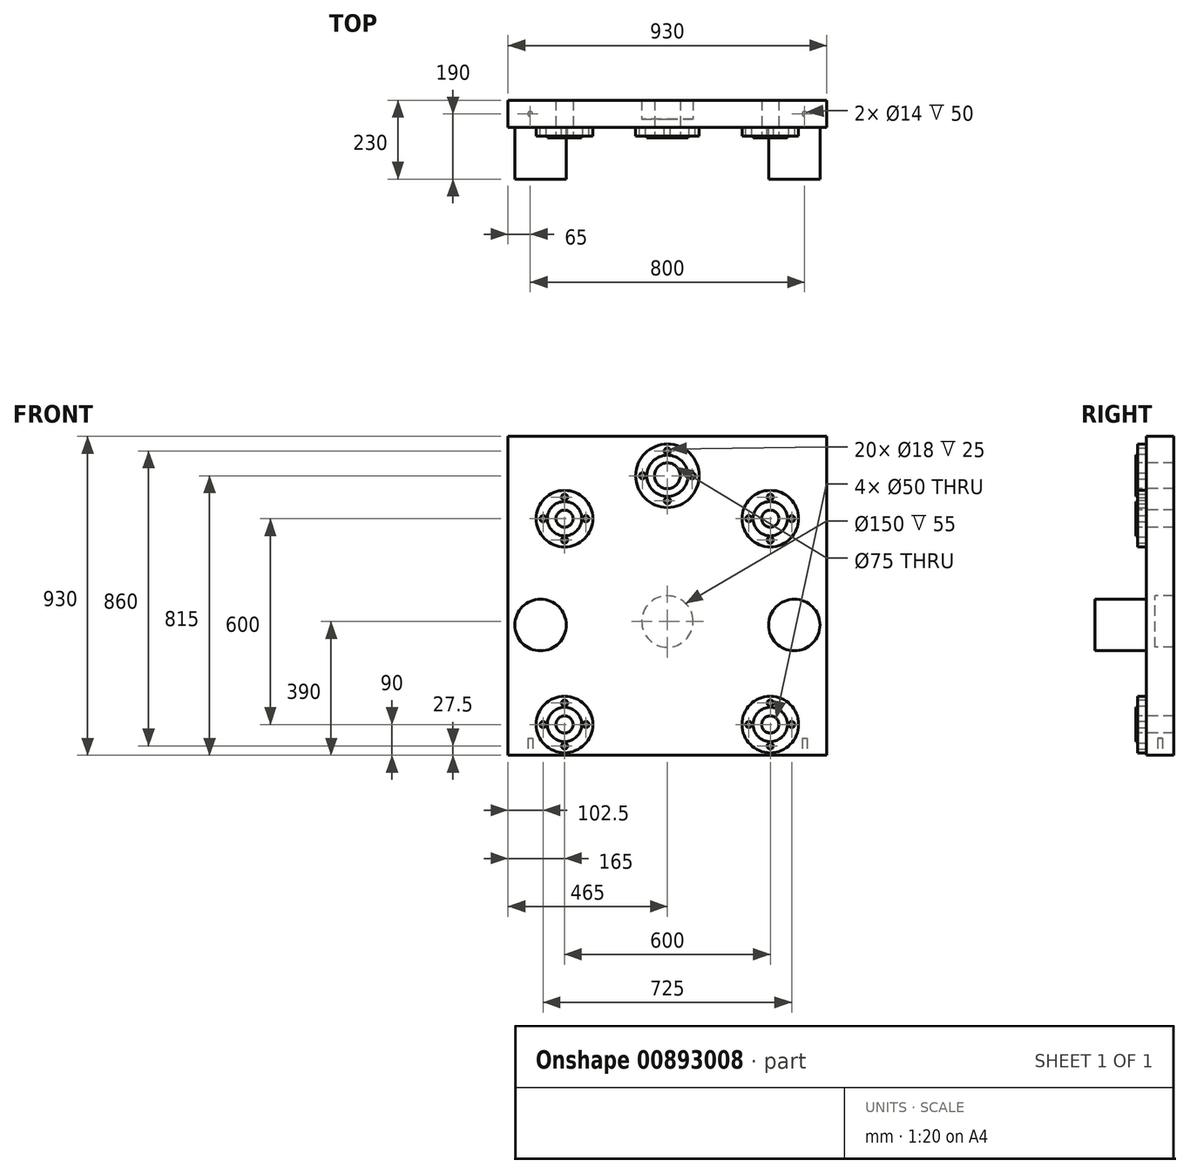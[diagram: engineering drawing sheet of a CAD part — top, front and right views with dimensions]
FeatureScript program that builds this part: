
annotation { "Feature Type Name" : "Feature", "Feature Type Description" : "" }
export const myFeature = defineFeature(function(context is Context, id is Id, definition is map)
    precondition{}
    {
        {
            var Q0;
            Q0=qCreatedBy(makeId("Front.planeOp"),FACE);
            var sketch = newSketch(context, id + "F0", { "sketchPlane" : qUnion([Q0])});
            skLineSegment(sketch, "E0.bottom", {"start": v(465, -965) * mm, "end": v(345, -965) * mm});
            skLineSegment(sketch, "E0.top", {"start": v(465, 965) * mm, "end": v(-465, 965) * mm});
            skLineSegment(sketch, "E0.left", {"start": v(465, -965) * mm, "end": v(465, 965) * mm});
            skLineSegment(sketch, "E0.right", {"start": v(-465, -965) * mm, "end": v(-465, 965) * mm});
            skPoint(sketch, "E0.middle", {"position": v(0, 0) * mm});
            skLineSegment(sketch, "E1.top", {"start": v(-345, -765) * mm, "end": v(345, -765) * mm});
            skLineSegment(sketch, "E1.left", {"start": v(-345, -965) * mm, "end": v(-345, -765) * mm});
            skLineSegment(sketch, "E1.right", {"start": v(345, -965) * mm, "end": v(345, -765) * mm});
            skLineSegment(sketch, "E2.bottom", {"start": v(-345, -645) * mm, "end": v(345, -645) * mm});
            skLineSegment(sketch, "E2.top", {"start": v(-345, -295) * mm, "end": v(345, -295) * mm});
            skLineSegment(sketch, "E2.left", {"start": v(-345, -645) * mm, "end": v(-345, -295) * mm});
            skLineSegment(sketch, "E2.right", {"start": v(345, -645) * mm, "end": v(345, -295) * mm});
            skLineSegment(sketch, "E3.trimOffspring", {"start": v(-345, -965) * mm, "end": v(-465, -965) * mm});
            skLineSegment(sketch, "E4.bottom", {"start": v(-345, -175) * mm, "end": v(345, -175) * mm});
            skLineSegment(sketch, "E4.top", {"start": v(-345, 25) * mm, "end": v(345, 25) * mm});
            skLineSegment(sketch, "E4.left", {"start": v(-345, -175) * mm, "end": v(-345, 25) * mm});
            skLineSegment(sketch, "E4.right", {"start": v(345, -175) * mm, "end": v(345, 25) * mm});
            skPoint(sketch, "E5.middle", {"position": v(0, 425) * mm});
            skSolve(sketch);
        }
        {
            var Q0;
            Q0=makeQuery(id+"F0.imprint","IMPRINT",FACE,{"disambiguationData":[TD([[makeQuery(id+"F0.imprint","IMPRINT",EDGE,{"derivedFrom":sQuery(id+"F0.wireOp",EDGE,"E0.bottom")}),-1.0]])]});
            extrude(context, id + "F1", {"entities" : qUnion([Q0]), "depth" : 80 * mm, "offsetDistance" : 25 * mm});
        }
        {
            var Q0;
            Q0=makeQuery(id+"F1.opExtrude","CAP_FACE",FACE,{"disambiguationData":[OSD([sQuery(id+"F0.wireOp",EDGE,"E0.bottom"),sQuery(id+"F0.wireOp",EDGE,"E0.top"),sQuery(id+"F0.wireOp",EDGE,"E0.left"),sQuery(id+"F0.wireOp",EDGE,"E0.right"),sQuery(id+"F0.wireOp",EDGE,"E1.top"),sQuery(id+"F0.wireOp",EDGE,"E1.left"),sQuery(id+"F0.wireOp",EDGE,"E1.right"),sQuery(id+"F0.wireOp",EDGE,"E2.bottom"),sQuery(id+"F0.wireOp",EDGE,"E2.top"),sQuery(id+"F0.wireOp",EDGE,"E2.left"),sQuery(id+"F0.wireOp",EDGE,"E2.right"),sQuery(id+"F0.wireOp",EDGE,"E3.trimOffspring"),sQuery(id+"F0.wireOp",EDGE,"nSGubIzk-R7de-6MO4-penA-cvBglKJnvsGC"),sQuery(id+"F0.wireOp",EDGE,"E4.bottom"),sQuery(id+"F0.wireOp",EDGE,"E4.top"),sQuery(id+"F0.wireOp",EDGE,"E4.left"),sQuery(id+"F0.wireOp",EDGE,"E4.right")])],"isStart":false});
            var sketch = newSketch(context, id + "F2", { "sketchPlane" : qUnion([Q0])});
            skCircle(sketch, "E6", {"center": v(-300, 125) * mm, "radius": 25 * mm});
            skCircle(sketch, "E7.0", {"center": v(0, 425) * mm, "radius": 75 * mm});
            skCircle(sketch, "E8.0.1.0", {"center": v(-300, 725) * mm, "radius": 25 * mm});
            skCircle(sketch, "E8.1.0.0", {"center": v(300, 125) * mm, "radius": 25 * mm});
            skCircle(sketch, "E8.1.1.0", {"center": v(300, 725) * mm, "radius": 25 * mm});
            skLineSegment(sketch, "E8.direction1", {"start": v(-300, 125) * mm, "end": v(300, 125) * mm, "construction": true});
            skLineSegment(sketch, "E8.direction2", {"start": v(-300, 125) * mm, "end": v(-300, 725) * mm, "construction": true});
            skSolve(sketch);
        }
        {
            var Q0;
            Q0=qSketchRegion(id+"F2",true);
            extrude(context, id + "F3", {"entities" : qUnion([Q0]), "operationType" : NewBodyOperationType.REMOVE, "oppositeDirection" : true, "depth" : 100 * mm, "offsetDistance" : 25 * mm});
        }
        {
            var Q0;
            Q0=makeQuery(id+"F1.opExtrude","CAP_FACE",FACE,{"disambiguationData":[OSD([sQuery(id+"F0.wireOp",EDGE,"E0.bottom"),sQuery(id+"F0.wireOp",EDGE,"E0.top"),sQuery(id+"F0.wireOp",EDGE,"E0.left"),sQuery(id+"F0.wireOp",EDGE,"E0.right"),sQuery(id+"F0.wireOp",EDGE,"E1.top"),sQuery(id+"F0.wireOp",EDGE,"E1.left"),sQuery(id+"F0.wireOp",EDGE,"E1.right"),sQuery(id+"F0.wireOp",EDGE,"E2.bottom"),sQuery(id+"F0.wireOp",EDGE,"E2.top"),sQuery(id+"F0.wireOp",EDGE,"E2.left"),sQuery(id+"F0.wireOp",EDGE,"E2.right"),sQuery(id+"F0.wireOp",EDGE,"E3.trimOffspring"),sQuery(id+"F0.wireOp",EDGE,"nSGubIzk-R7de-6MO4-penA-cvBglKJnvsGC"),sQuery(id+"F0.wireOp",EDGE,"E4.bottom"),sQuery(id+"F0.wireOp",EDGE,"E4.top"),sQuery(id+"F0.wireOp",EDGE,"E4.left"),sQuery(id+"F0.wireOp",EDGE,"E4.right")])],"isStart":false});
            var sketch = newSketch(context, id + "F4", { "sketchPlane" : qUnion([Q0])});
            skCircle(sketch, "E9", {"center": v(-370, 415) * mm, "radius": 75 * mm});
            skCircle(sketch, "E10.MirrorC", {"center": v(370, 415) * mm, "radius": 75 * mm});
            skSolve(sketch);
        }
        {
            var Q0;
            Q0=qSketchRegion(id+"F4",true);
            extrude(context, id + "F5", {"entities" : qUnion([Q0]), "operationType" : NewBodyOperationType.ADD, "depth" : 150 * mm, "offsetDistance" : 25 * mm});
        }
        {
            var Q0;
            Q0=makeQuery(id+"F1.opExtrude","CAP_FACE",FACE,{"disambiguationData":[OSD([sQuery(id+"F0.wireOp",EDGE,"E0.bottom"),sQuery(id+"F0.wireOp",EDGE,"E0.top"),sQuery(id+"F0.wireOp",EDGE,"E0.left"),sQuery(id+"F0.wireOp",EDGE,"E0.right"),sQuery(id+"F0.wireOp",EDGE,"E1.top"),sQuery(id+"F0.wireOp",EDGE,"E1.left"),sQuery(id+"F0.wireOp",EDGE,"E1.right"),sQuery(id+"F0.wireOp",EDGE,"E2.bottom"),sQuery(id+"F0.wireOp",EDGE,"E2.top"),sQuery(id+"F0.wireOp",EDGE,"E2.left"),sQuery(id+"F0.wireOp",EDGE,"E2.right"),sQuery(id+"F0.wireOp",EDGE,"E3.trimOffspring"),sQuery(id+"F0.wireOp",EDGE,"nSGubIzk-R7de-6MO4-penA-cvBglKJnvsGC"),sQuery(id+"F0.wireOp",EDGE,"E4.bottom"),sQuery(id+"F0.wireOp",EDGE,"E4.top"),sQuery(id+"F0.wireOp",EDGE,"E4.left"),sQuery(id+"F0.wireOp",EDGE,"E4.right")])],"isStart":false});
            var sketch = newSketch(context, id + "F6", { "sketchPlane" : qUnion([Q0])});
            skCircle(sketch, "E11", {"center": v(-300, 725) * mm, "radius": 82.5 * mm});
            skCircle(sketch, "E12", {"center": v(-300, 787.5) * mm, "radius": 9 * mm});
            skCircle(sketch, "E13.0", {"center": v(-300, 725) * mm, "radius": 25 * mm});
            skCircle(sketch, "E14.1.0", {"center": v(-362.5, 725) * mm, "radius": 9 * mm});
            skCircle(sketch, "E14.2.0", {"center": v(-300, 662.5) * mm, "radius": 9 * mm});
            skCircle(sketch, "E14.3.0", {"center": v(-237.5, 725) * mm, "radius": 9 * mm});
            skPoint(sketch, "E15.0.1.0", {"position": v(-300, 125) * mm});
            skCircle(sketch, "E15.0.1.1", {"center": v(-300, 125) * mm, "radius": 82.5 * mm});
            skCircle(sketch, "E15.0.1.2", {"center": v(-300, 125) * mm, "radius": 25 * mm});
            skCircle(sketch, "E15.0.1.3", {"center": v(-237.5, 125) * mm, "radius": 9 * mm});
            skCircle(sketch, "E15.0.1.4", {"center": v(-362.5, 125) * mm, "radius": 9 * mm});
            skCircle(sketch, "E15.0.1.5", {"center": v(-300, 187.5) * mm, "radius": 9 * mm});
            skCircle(sketch, "E15.0.1.6", {"center": v(-300, 62.5) * mm, "radius": 9 * mm});
            skPoint(sketch, "E15.1.0.0", {"position": v(300, 725) * mm});
            skCircle(sketch, "E15.1.0.1", {"center": v(300, 725) * mm, "radius": 82.5 * mm});
            skCircle(sketch, "E15.1.0.2", {"center": v(300, 725) * mm, "radius": 25 * mm});
            skCircle(sketch, "E15.1.0.3", {"center": v(362.5, 725) * mm, "radius": 9 * mm});
            skCircle(sketch, "E15.1.0.4", {"center": v(237.5, 725) * mm, "radius": 9 * mm});
            skCircle(sketch, "E15.1.0.5", {"center": v(300, 787.5) * mm, "radius": 9 * mm});
            skCircle(sketch, "E15.1.0.6", {"center": v(300, 662.5) * mm, "radius": 9 * mm});
            skPoint(sketch, "E15.1.1.0", {"position": v(300, 125) * mm});
            skCircle(sketch, "E15.1.1.1", {"center": v(300, 125) * mm, "radius": 82.5 * mm});
            skCircle(sketch, "E15.1.1.2", {"center": v(300, 125) * mm, "radius": 25 * mm});
            skCircle(sketch, "E15.1.1.3", {"center": v(362.5, 125) * mm, "radius": 9 * mm});
            skCircle(sketch, "E15.1.1.4", {"center": v(237.5, 125) * mm, "radius": 9 * mm});
            skCircle(sketch, "E15.1.1.5", {"center": v(300, 187.5) * mm, "radius": 9 * mm});
            skCircle(sketch, "E15.1.1.6", {"center": v(300, 62.5) * mm, "radius": 9 * mm});
            skLineSegment(sketch, "E15.direction1", {"start": v(-300, 662.5) * mm, "end": v(300, 662.5) * mm, "construction": true});
            skLineSegment(sketch, "E15.direction2", {"start": v(-300, 662.5) * mm, "end": v(-300, 62.5) * mm, "construction": true});
            skSolve(sketch);
        }
        {
            var Q0;
            Q0=qSketchRegion(id+"F6",true);
            extrude(context, id + "F7", {"entities" : qUnion([Q0]), "operationType" : NewBodyOperationType.ADD, "depth" : 25 * mm, "offsetDistance" : 25 * mm});
        }
        {
            var Q0;
            Q0=makeQuery(id+"F7.opExtrude","CAP_FACE",FACE,{"disambiguationData":[OSD([sQuery(id+"F6.wireOp",EDGE,"E11"),sQuery(id+"F6.wireOp",EDGE,"E12"),sQuery(id+"F6.wireOp",EDGE,"E13.0"),sQuery(id+"F6.wireOp",EDGE,"E14.1.0"),sQuery(id+"F6.wireOp",EDGE,"E14.2.0"),sQuery(id+"F6.wireOp",EDGE,"E14.3.0")])],"isStart":false});
            var sketch = newSketch(context, id + "F8", { "sketchPlane" : qUnion([Q0])});
            skCircle(sketch, "E16", {"center": v(-300, 725) * mm, "radius": 50 * mm});
            skCircle(sketch, "E17.0.1.0", {"center": v(-300, 125) * mm, "radius": 50 * mm});
            skCircle(sketch, "E17.1.0.0", {"center": v(300, 725) * mm, "radius": 50 * mm});
            skCircle(sketch, "E17.1.1.0", {"center": v(300, 125) * mm, "radius": 50 * mm});
            skLineSegment(sketch, "E17.direction1", {"start": v(-300, 725) * mm, "end": v(300, 725) * mm, "construction": true});
            skLineSegment(sketch, "E17.direction2", {"start": v(-300, 725) * mm, "end": v(-300, 125) * mm, "construction": true});
            skCircle(sketch, "E18", {"center": v(300, 725) * mm, "radius": 25 * mm});
            skCircle(sketch, "E19", {"center": v(300, 125) * mm, "radius": 25 * mm});
            skCircle(sketch, "E20", {"center": v(-300, 125) * mm, "radius": 25 * mm});
            skCircle(sketch, "E21", {"center": v(-300, 725) * mm, "radius": 25 * mm});
            skSolve(sketch);
        }
        {
            var Q0;
            Q0=qSketchRegion(id+"F8",true);
            extrude(context, id + "F9", {"entities" : qUnion([Q0]), "operationType" : NewBodyOperationType.ADD, "depth" : 5 * mm, "offsetDistance" : 25 * mm});
        }
        {
            var Q0;
            {var subQ0=sQuery(id+"F0.wireOp",EDGE,"E4.right");var subQ1=sQuery(id+"F0.wireOp",EDGE,"E4.left");var subQ2=sQuery(id+"F0.wireOp",EDGE,"E4.top");var subQ3=sQuery(id+"F0.wireOp",EDGE,"E1.left");var subQ4=sQuery(id+"F0.wireOp",EDGE,"E4.bottom");var subQ5=sQuery(id+"F0.wireOp",EDGE,"E3.trimOffspring");var subQ6=sQuery(id+"F0.wireOp",EDGE,"E2.right");var subQ7=sQuery(id+"F0.wireOp",EDGE,"E0.left");var subQ8=sQuery(id+"F0.wireOp",EDGE,"E0.top");var subQ9=sQuery(id+"F0.wireOp",EDGE,"E0.right");var subQ10=sQuery(id+"F0.wireOp",EDGE,"E2.bottom");var subQ11=sQuery(id+"F0.wireOp",EDGE,"E0.bottom");var subQ12=sQuery(id+"F0.wireOp",EDGE,"E2.left");var subQ13=sQuery(id+"F0.wireOp",EDGE,"E1.top");var subQ14=sQuery(id+"F0.wireOp",EDGE,"E1.right");var subQ15=sQuery(id+"F0.wireOp",EDGE,"E2.top");Q0=makeQuery(id+"F7.boolean.opBoolean","SPLIT",FACE,{"disambiguationData":[TD([makeQuery(id+"F1.opExtrude","SWEPT_FACE",FACE,{"disambiguationData":[OSD([subQ11])]})])],"derivedFrom":makeQuery(id+"F1.opExtrude","CAP_FACE",FACE,{"disambiguationData":[OSD([subQ11,subQ8,subQ7,subQ9,subQ13,subQ3,subQ14,subQ10,subQ15,subQ12,subQ6,subQ5,subQ4,subQ2,subQ1,subQ0])],"isStart":false})});}
            var sketch = newSketch(context, id + "F10", { "sketchPlane" : qUnion([Q0])});
            skCircle(sketch, "E22.0", {"center": v(0, 425) * mm, "radius": 75 * mm});
            skSolve(sketch);
        }
        {
            var Q0;
            Q0=qSketchRegion(id+"F10",true);
            extrude(context, id + "F11", {"entities" : qUnion([Q0]), "operationType" : NewBodyOperationType.ADD, "oppositeDirection" : true, "depth" : 25 * mm, "offsetDistance" : 25 * mm});
        }
        {
            var Q0;
            {var subQ0=sQuery(id+"F0.wireOp",EDGE,"E4.right");var subQ1=sQuery(id+"F0.wireOp",EDGE,"E4.left");var subQ2=sQuery(id+"F0.wireOp",EDGE,"E4.top");var subQ3=sQuery(id+"F0.wireOp",EDGE,"E1.left");var subQ4=sQuery(id+"F0.wireOp",EDGE,"E4.bottom");var subQ5=sQuery(id+"F0.wireOp",EDGE,"E3.trimOffspring");var subQ6=sQuery(id+"F0.wireOp",EDGE,"E2.right");var subQ7=sQuery(id+"F0.wireOp",EDGE,"E0.left");var subQ8=sQuery(id+"F0.wireOp",EDGE,"E0.top");var subQ9=sQuery(id+"F0.wireOp",EDGE,"E0.right");var subQ10=sQuery(id+"F0.wireOp",EDGE,"E2.bottom");var subQ11=sQuery(id+"F0.wireOp",EDGE,"E0.bottom");var subQ12=sQuery(id+"F0.wireOp",EDGE,"E2.left");var subQ13=sQuery(id+"F0.wireOp",EDGE,"E1.top");var subQ14=sQuery(id+"F0.wireOp",EDGE,"E1.right");var subQ15=sQuery(id+"F0.wireOp",EDGE,"E2.top");Q0=makeQuery(id+"F11.boolean.opBoolean","MERGE",FACE,{"derivedFrom":[makeQuery(id+"F7.boolean.opBoolean","SPLIT",FACE,{"disambiguationData":[TD([makeQuery(id+"F1.opExtrude","SWEPT_FACE",FACE,{"disambiguationData":[OSD([subQ11])]})])],"derivedFrom":makeQuery(id+"F1.opExtrude","CAP_FACE",FACE,{"disambiguationData":[OSD([subQ11,subQ8,subQ7,subQ9,subQ13,subQ3,subQ14,subQ10,subQ15,subQ12,subQ6,subQ5,subQ4,subQ2,subQ1,subQ0])],"isStart":false})}),makeQuery(id+"F11.opExtrude","CAP_FACE",FACE,{"disambiguationData":[OSD([sQuery(id+"F10.wireOp",EDGE,"E22.0")])],"isStart":true})]});}
            var sketch = newSketch(context, id + "F12", { "sketchPlane" : qUnion([Q0])});
            skCircle(sketch, "E23", {"center": v(0, 850) * mm, "radius": 37.5 * mm});
            skPoint(sketch, "E23.centerSnap0", {"position": v(0, 965) * mm});
            skCircle(sketch, "E24.0", {"center": v(300, 725) * mm, "radius": 25 * mm});
            skSolve(sketch);
        }
        {
            var Q0;
            Q0=makeQuery(id+"F12.imprint","IMPRINT",FACE,{"disambiguationData":[TD([[makeQuery(id+"F12.imprint","IMPRINT",EDGE,{"derivedFrom":sQuery(id+"F12.wireOp",EDGE,"E23")}),1.0]])]});
            extrude(context, id + "F13", {"entities" : qUnion([Q0]), "operationType" : NewBodyOperationType.REMOVE, "oppositeDirection" : true, "depth" : 100 * mm, "offsetDistance" : 25 * mm});
        }
        {
            var Q0;
            {var subQ0=sQuery(id+"F0.wireOp",EDGE,"E4.right");var subQ1=sQuery(id+"F0.wireOp",EDGE,"E4.left");var subQ2=sQuery(id+"F0.wireOp",EDGE,"E4.top");var subQ3=sQuery(id+"F0.wireOp",EDGE,"E1.left");var subQ4=sQuery(id+"F0.wireOp",EDGE,"E4.bottom");var subQ5=sQuery(id+"F0.wireOp",EDGE,"E3.trimOffspring");var subQ6=sQuery(id+"F0.wireOp",EDGE,"E2.right");var subQ7=sQuery(id+"F0.wireOp",EDGE,"E0.left");var subQ8=sQuery(id+"F0.wireOp",EDGE,"E0.top");var subQ9=sQuery(id+"F0.wireOp",EDGE,"E0.right");var subQ10=sQuery(id+"F0.wireOp",EDGE,"E2.bottom");var subQ11=sQuery(id+"F0.wireOp",EDGE,"E0.bottom");var subQ12=sQuery(id+"F0.wireOp",EDGE,"E2.left");var subQ13=sQuery(id+"F0.wireOp",EDGE,"E1.top");var subQ14=sQuery(id+"F0.wireOp",EDGE,"E1.right");var subQ15=sQuery(id+"F0.wireOp",EDGE,"E2.top");Q0=makeQuery(id+"F11.boolean.opBoolean","MERGE",FACE,{"derivedFrom":[makeQuery(id+"F7.boolean.opBoolean","SPLIT",FACE,{"disambiguationData":[TD([makeQuery(id+"F1.opExtrude","SWEPT_FACE",FACE,{"disambiguationData":[OSD([subQ11])]})])],"derivedFrom":makeQuery(id+"F1.opExtrude","CAP_FACE",FACE,{"disambiguationData":[OSD([subQ11,subQ8,subQ7,subQ9,subQ13,subQ3,subQ14,subQ10,subQ15,subQ12,subQ6,subQ5,subQ4,subQ2,subQ1,subQ0])],"isStart":false})}),makeQuery(id+"F11.opExtrude","CAP_FACE",FACE,{"disambiguationData":[OSD([sQuery(id+"F10.wireOp",EDGE,"E22.0")])],"isStart":true})]});}
            var sketch = newSketch(context, id + "F14", { "sketchPlane" : qUnion([Q0])});
            skCircle(sketch, "E25", {"center": v(0, 850) * mm, "radius": 92.5 * mm});
            skCircle(sketch, "E26", {"center": v(0, 922.5) * mm, "radius": 9 * mm});
            skCircle(sketch, "E27.1.0", {"center": v(-72.5, 850) * mm, "radius": 9 * mm});
            skCircle(sketch, "E27.2.0", {"center": v(0, 777.5) * mm, "radius": 9 * mm});
            skCircle(sketch, "E27.3.0", {"center": v(72.5, 850) * mm, "radius": 9 * mm});
            skSolve(sketch);
        }
        {
            var Q0;
            Q0=makeQuery(id+"F14.imprint","IMPRINT",FACE,{"disambiguationData":[TD([[makeQuery(id+"F14.imprint","IMPRINT",EDGE,{"derivedFrom":sQuery(id+"F14.wireOp",EDGE,"E25")}),1.0]])]});
            extrude(context, id + "F15", {"entities" : qUnion([Q0]), "operationType" : NewBodyOperationType.ADD, "depth" : 25 * mm, "offsetDistance" : 25 * mm});
        }
        {
            var Q0;
            Q0=makeQuery(id+"F15.opExtrude","CAP_FACE",FACE,{"disambiguationData":[OSD([sQuery(id+"F12.wireOp",EDGE,"E23"),sQuery(id+"F14.wireOp",EDGE,"E25"),sQuery(id+"F14.wireOp",EDGE,"E26"),sQuery(id+"F14.wireOp",EDGE,"E27.1.0"),sQuery(id+"F14.wireOp",EDGE,"E27.2.0"),sQuery(id+"F14.wireOp",EDGE,"E27.3.0")])],"isStart":false});
            var sketch = newSketch(context, id + "F16", { "sketchPlane" : qUnion([Q0])});
            skCircle(sketch, "E28", {"center": v(0, 850) * mm, "radius": 60 * mm});
            skSolve(sketch);
        }
        {
            var Q0;
            Q0=makeQuery(id+"F16.imprint","IMPRINT",FACE,{"disambiguationData":[TD([[makeQuery(id+"F16.imprint","IMPRINT",EDGE,{"derivedFrom":sQuery(id+"F16.wireOp",EDGE,"E28")}),1.0]])]});
            extrude(context, id + "F17", {"entities" : qUnion([Q0]), "operationType" : NewBodyOperationType.ADD, "depth" : 5 * mm, "offsetDistance" : 25 * mm});
        }
        {
            var Q0;
            {var subQ2=sQuery(id+"F0.wireOp",EDGE,"E4.right");var subQ5=sQuery(id+"F0.wireOp",EDGE,"E4.left");var subQ8=sQuery(id+"F0.wireOp",EDGE,"E4.top");var subQ10=sQuery(id+"F0.wireOp",EDGE,"E4.bottom");var subQ12=sQuery(id+"F0.wireOp",EDGE,"E3.trimOffspring");var subQ14=sQuery(id+"F0.wireOp",EDGE,"E2.right");var subQ16=sQuery(id+"F0.wireOp",EDGE,"E0.left");var subQ18=sQuery(id+"F0.wireOp",EDGE,"E0.top");var subQ20=sQuery(id+"F0.wireOp",EDGE,"E0.right");var subQ23=sQuery(id+"F0.wireOp",EDGE,"E2.bottom");var subQ25=sQuery(id+"F0.wireOp",EDGE,"E0.bottom");var subQ26=makeQuery(id+"F1.opExtrude","SWEPT_FACE",FACE,{"disambiguationData":[OSD([subQ25])]});var subQ27=sQuery(id+"F0.wireOp",EDGE,"E2.left");var subQ29=sQuery(id+"F0.wireOp",EDGE,"E1.top");var subQ32=sQuery(id+"F0.wireOp",EDGE,"E1.left");var subQ34=sQuery(id+"F0.wireOp",EDGE,"E1.right");var subQ36=sQuery(id+"F0.wireOp",EDGE,"E2.top");Q0=makeQuery(id+"F15.boolean.opBoolean","SPLIT",FACE,{"disambiguationData":[TD([subQ26])],"derivedFrom":makeQuery(id+"F11.boolean.opBoolean","MERGE",FACE,{"derivedFrom":[makeQuery(id+"F7.boolean.opBoolean","SPLIT",FACE,{"disambiguationData":[TD([subQ26])],"derivedFrom":makeQuery(id+"F1.opExtrude","CAP_FACE",FACE,{"disambiguationData":[OSD([subQ25,subQ18,subQ16,subQ20,subQ29,subQ32,subQ34,subQ23,subQ36,subQ27,subQ14,subQ12,subQ10,subQ8,subQ5,subQ2])],"isStart":false})}),makeQuery(id+"F11.opExtrude","CAP_FACE",FACE,{"disambiguationData":[OSD([sQuery(id+"F10.wireOp",EDGE,"E22.0")])],"isStart":true})]})});}
            var sketch = newSketch(context, id + "F18", { "sketchPlane" : qUnion([Q0])});
            skLineSegment(sketch, "E29.bottom", {"start": v(-465, -965) * mm, "end": v(465, -965) * mm});
            skLineSegment(sketch, "E29.top", {"start": v(-465, 35) * mm, "end": v(465, 35) * mm});
            skLineSegment(sketch, "E29.left", {"start": v(-465, -965) * mm, "end": v(-465, 35) * mm});
            skLineSegment(sketch, "E29.right", {"start": v(465, -965) * mm, "end": v(465, 35) * mm});
            skSolve(sketch);
        }
        {
            var Q0;
            Q0=qSketchRegion(id+"F18",true);
            extrude(context, id + "F19", {"entities" : qUnion([Q0]), "operationType" : NewBodyOperationType.REMOVE, "oppositeDirection" : true, "depth" : 100 * mm, "offsetDistance" : 25 * mm});
        }
        {
            var Q0;
            Q0=makeQuery(id+"F19.boolean.opBoolean","COPY",FACE,{"derivedFrom":makeQuery(id+"F19.opExtrude","SWEPT_FACE",FACE,{"disambiguationData":[OSD([sQuery(id+"F18.wireOp",EDGE,"E29.top")])]})});
            var sketch = newSketch(context, id + "F20", { "sketchPlane" : qUnion([Q0])});
            skCircle(sketch, "E30", {"center": v(-400, 40) * mm, "radius": 7 * mm});
            skCircle(sketch, "E31.MirrorC", {"center": v(400, 40) * mm, "radius": 7 * mm});
            skSolve(sketch);
        }
        {
            var Q0;
            Q0=qSketchRegion(id+"F20",true);
            extrude(context, id + "F21", {"entities" : qUnion([Q0]), "operationType" : NewBodyOperationType.REMOVE, "oppositeDirection" : true, "depth" : 50 * mm, "offsetDistance" : 25 * mm});
        }
    });
